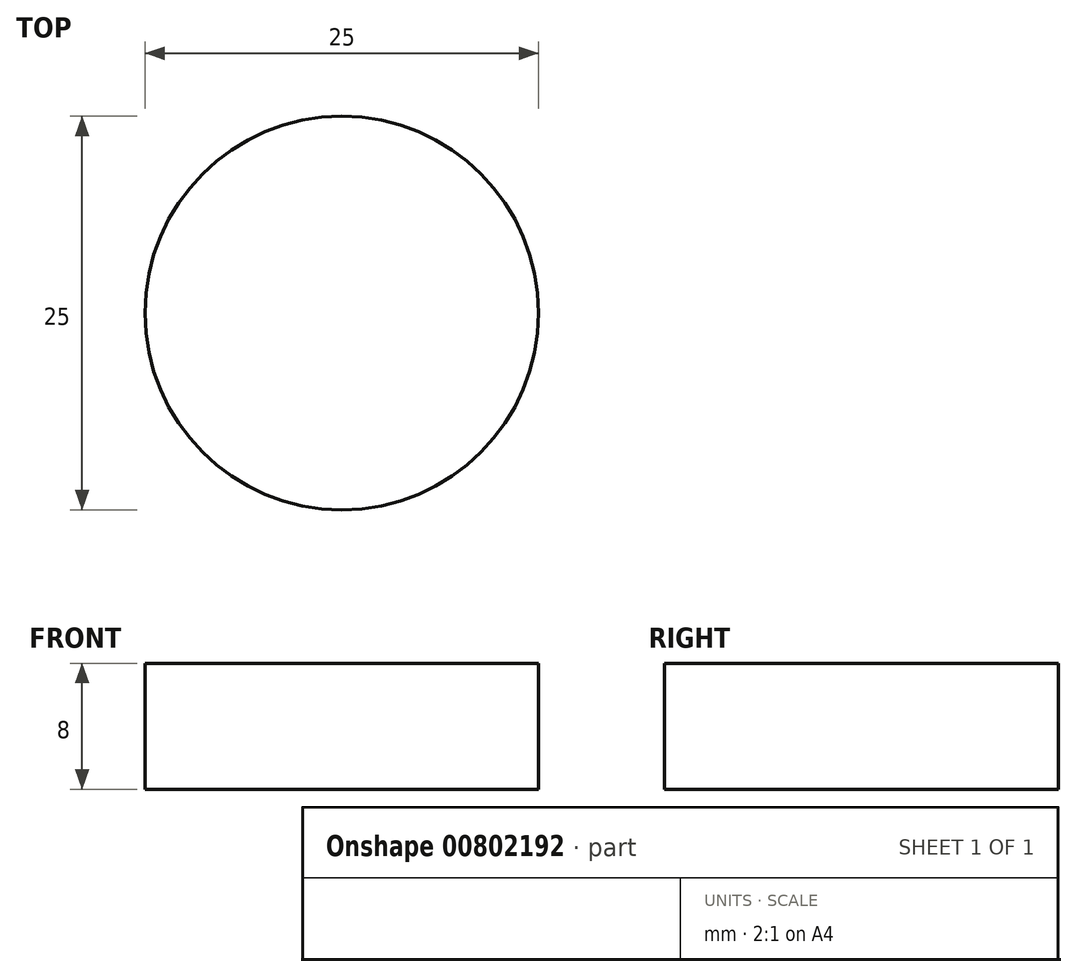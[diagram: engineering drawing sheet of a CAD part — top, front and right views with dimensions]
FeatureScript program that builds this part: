
annotation { "Feature Type Name" : "Feature", "Feature Type Description" : "" }
export const myFeature = defineFeature(function(context is Context, id is Id, definition is map)
    precondition{}
    {
        {
            var Q0;
            Q0=qCreatedBy(makeId("Top.planeOp"),FACE);
            var sketch = newSketch(context, id + "F0", { "sketchPlane" : qUnion([Q0])});
            skCircle(sketch, "E0", {"center": v(0, 0) * mm, "radius": 12.5 * mm});
            skSolve(sketch);
        }
        {
            var Q0;
            Q0 = qSketchRegion(id + "F0", true);
            extrude(context, id + "F1", {"entities" : qUnion([Q0]), "depth" : 8 * mm, "offsetDistance" : 25 * mm});
        }
    });
